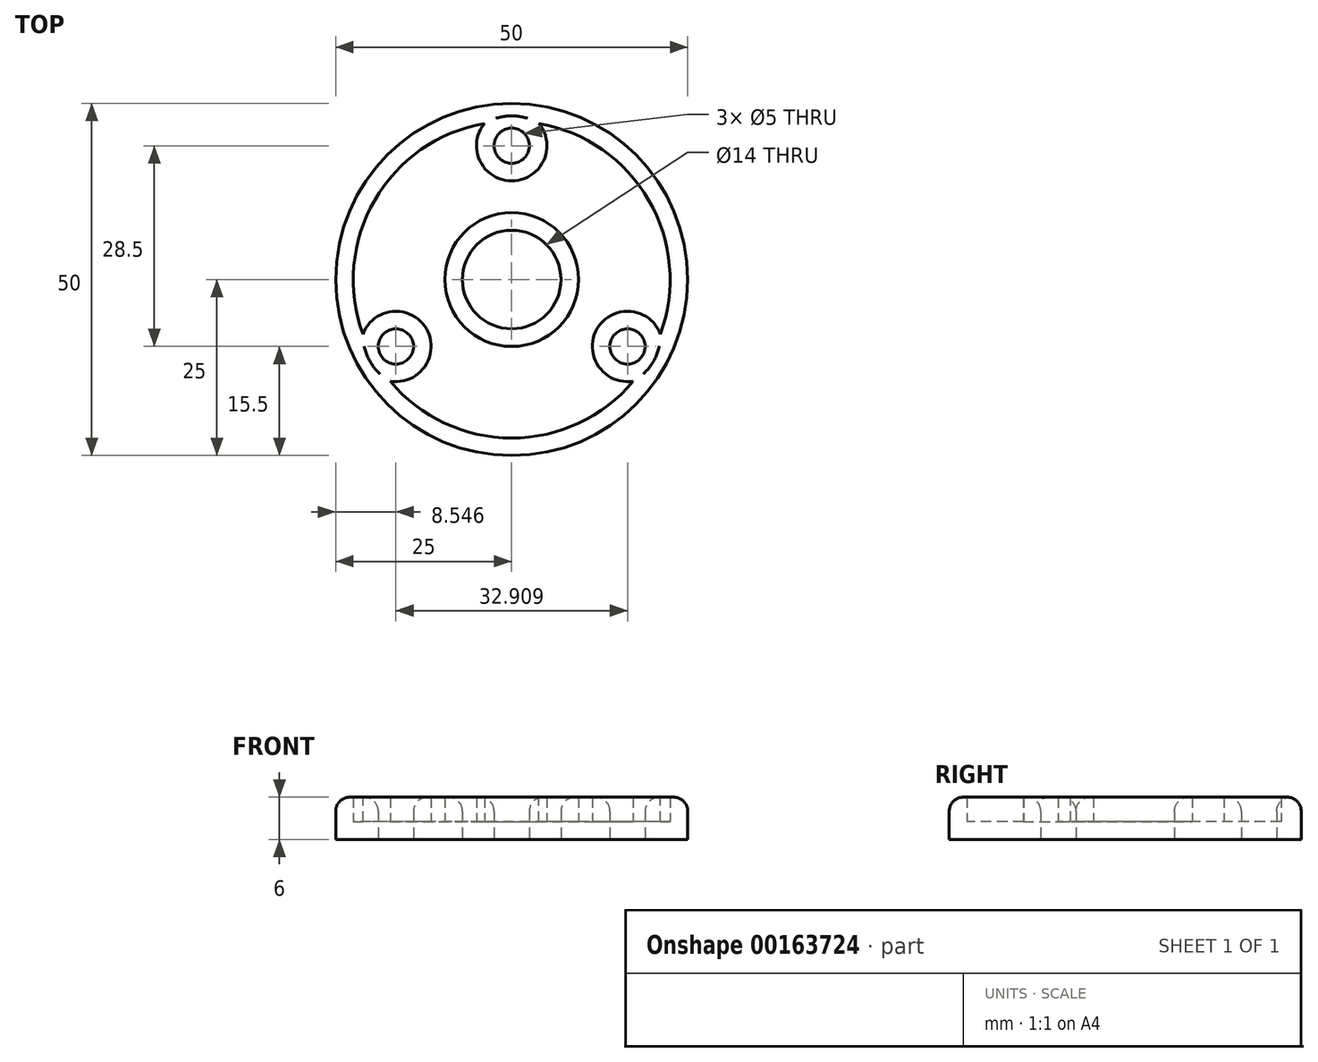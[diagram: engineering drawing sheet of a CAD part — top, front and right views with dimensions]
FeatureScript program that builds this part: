
annotation { "Feature Type Name" : "Feature", "Feature Type Description" : "" }
export const myFeature = defineFeature(function(context is Context, id is Id, definition is map)
    precondition{}
    {
        {
            var Q0;
            Q0=qCreatedBy(makeId("Top.planeOp"),FACE);
            var sketch = newSketch(context, id + "F0", { "sketchPlane" : qUnion([Q0])});
            skCircle(sketch, "E0", {"center": v(0, 0) * mm, "radius": 25 * mm});
            skCircle(sketch, "E1", {"center": v(0, 0) * mm, "radius": 7 * mm});
            skCircle(sketch, "E2", {"center": v(0, 0) * mm, "radius": 19 * mm, "construction": true});
            skLineSegment(sketch, "E3", {"start": v(0, 0) * mm, "end": v(-21.65, -12.5) * mm, "construction": true});
            skCircle(sketch, "E4", {"center": v(-16.45, -9.5) * mm, "radius": 2.5 * mm});
            skLineSegment(sketch, "E5", {"start": v(0, 0) * mm, "end": v(16.45, -9.5) * mm});
            skCircle(sketch, "E6.1.0", {"center": v(0, 19) * mm, "radius": 2.5 * mm});
            skCircle(sketch, "E6.2.0", {"center": v(16.45, -9.5) * mm, "radius": 2.5 * mm});
            skLineSegment(sketch, "E6.anchor1", {"start": v(0, 0) * mm, "end": v(-16.45, -9.5) * mm, "construction": true});
            skLineSegment(sketch, "E6.anchor2", {"start": v(0, 0) * mm, "end": v(16.45, -9.5) * mm, "construction": true});
            skSolve(sketch);
        }
        {
            var Q0;
            Q0 = qSketchRegion(id + "F0", true);
            extrude(context, id + "F1", {"entities" : qUnion([Q0]), "depth" : 6 * mm});
        }
        {
            var Q0;
            Q0=makeQuery(id+"F1.opExtrude","CAP_EDGE",EDGE,{"disambiguationData":[OSD([sQuery(id+"F0.wireOp",EDGE,"E0")])],"isStart":false});
            var Q1;
            Q1=makeQuery(id+"F1.opExtrude","CAP_EDGE",EDGE,{"disambiguationData":[OSD([sQuery(id+"F0.wireOp",EDGE,"E4")])],"isStart":false});
            var Q2;
            Q2=makeQuery(id+"F1.opExtrude","CAP_EDGE",EDGE,{"disambiguationData":[OSD([sQuery(id+"F0.wireOp",EDGE,"E1")])],"isStart":false});
            var Q3;
            Q3=makeQuery(id+"F1.opExtrude","CAP_EDGE",EDGE,{"disambiguationData":[OSD([sQuery(id+"F0.wireOp",EDGE,"E6.1.0")])],"isStart":false});
            var Q4;
            Q4=makeQuery(id+"F1.opExtrude","CAP_EDGE",EDGE,{"disambiguationData":[OSD([sQuery(id+"F0.wireOp",EDGE,"E6.2.0")])],"isStart":false});
            fillet(context, id + "F2", {"entities" : qUnion([Q0, Q1, Q2, Q3, Q4]), "radius" : 2 * mm, "tangentPropagation" : true, "allowEdgeOverflow" : false});
        }
        {
            var Q0;
            Q0=makeQuery(id+"F1.opExtrude","CAP_FACE",FACE,{"disambiguationData":[OSD([sQuery(id+"F0.wireOp",EDGE,"E0"),sQuery(id+"F0.wireOp",EDGE,"E1"),sQuery(id+"F0.wireOp",EDGE,"E4"),sQuery(id+"F0.wireOp",EDGE,"E6.1.0"),sQuery(id+"F0.wireOp",EDGE,"E6.2.0")])],"isStart":false});
            shell(context, id + "F3", {"entities" : qUnion([Q0]), "thickness" : 2.5 * mm});
        }
    });
